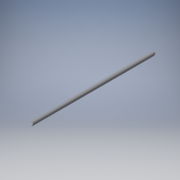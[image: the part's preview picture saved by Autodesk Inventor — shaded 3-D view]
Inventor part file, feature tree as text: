
AUTODESK INVENTOR PART (.ipt)
format: ipt  version: 2016 (Build 200138000, 138)  size: 86,528 bytes
history: native  units: in
note: dims shown in document units (in); Inventor stores cm internally (conversion verified against a paired STEP export)
features: extrude x1, sketch x1
ambient origin geometry x8: Origin, YZ Plane, XZ Plane, XY Plane, X Axis, Y Axis, Z Axis, Center Point
bodies: Solid1 (feature_tree)
feature tree (2):
  extrude  "Extrusion1"  Depth=8.0in TaperAngle=0.0deg
  sketch  "Sketch1"  dims[d0=0.188in d1=8.0in d2=0.0in]
